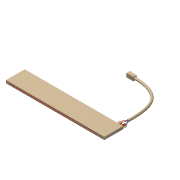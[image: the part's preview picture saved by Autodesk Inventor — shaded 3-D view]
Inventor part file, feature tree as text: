
AUTODESK INVENTOR PART (.ipt)
format: ipt  version: 2015 SP1 (Build 190203100, 203)  size: 430,080 bytes
history: native  units: mm
features: sketch x18, extrude x10, projected_geometry x10, sweep x5, plane x4, fillet x2
ambient origin geometry x8: Origin, YZ Plane, XZ Plane, XY Plane, X Axis, Y Axis, Z Axis, Center Point
bodies: Solid1 (feature_tree)
feature tree (49):
  sketch  "Sketch1"  dims[d0=210.0mm d1=40.0mm]
  extrude  "Extrusion1"  Depth=40.0mm
  extrude  "Extrusion2"  Depth=5.0mm
  extrude  "Extrusion3"  Depth=5.0mm
  extrude  "Extrusion4"  Depth=5.0mm
  extrude  "Extrusion5"  Depth=40.0mm
  extrude  "Extrusion6"  Depth=15.909903mm
  sketch  "Sketch6"  dims[d10=5.0mm d11=15.909903mm]
  plane  "Work Plane1"
  sketch  "Sketch7"  dims[d12=31.819805mm d13=15.909903mm]
  sketch  "Sketch9"  dims[d14=1.0mm d15=0.0mm d16=1.0mm d17=0.0mm]
  sketch  "Sketch10"  dims[d18=1.0mm d19=0.0mm d20=1.0mm d21=0.0mm]
  sketch  "Sketch11"  dims[d22=1.0mm d23=0.0mm d24=1.0mm d25=0.0mm]
  sketch  "Sketch12"  dims[d26=2.0mm d27=2.5mm]
  plane  "Work Plane3"
  plane  "Work Plane4"
  sketch  "Sketch13"  dims[d28=10.0mm d29=5.0mm]
  sketch  "Sketch14"  dims[d30=10.0mm d31=5.0mm]
  plane  "Work Plane5"
  sketch  "Sketch15"  dims[d32=0.8mm d33=0.8mm]
  sweep  "Sweep1"
  sweep  "Sweep2"
  sweep  "Sweep3"
  sweep  "Sweep4"
  sweep  "Sweep5"
  extrude  "Extrusion7"  Depth=5.0mm
  extrude  "Extrusion8"  Depth=5.0mm
  extrude  "Extrusion9"  Depth=0.8mm
  extrude  "Extrusion10"  Depth=0.8mm
  fillet  "Fillet1"  [1 undecoded]
  fillet  "Fillet2"  [1 undecoded]
  sketch  "Sketch2"  dims[d2=8.0mm d3=5.0mm]
  projected_geometry  "Projected Loop1"
  sketch  "Sketch3"  dims[d4=5.0mm d5=5.0mm]
  projected_geometry  "Projected Loop2"
  sketch  "Sketch4"  dims[d6=5.0mm d7=5.0mm]
  projected_geometry  "Projected Loop3"
  projected_geometry  "Projected Loop4"
  projected_geometry  "Projected Loop5"
  sketch  "Sketch5"  dims[d8=40.0mm d9=40.0mm]
  projected_geometry  "Projected Loop6"
  projected_geometry  "Projected Loop7"
  projected_geometry  "Projected Loop8"
  sketch  "Sketch16"  dims[d34=0.8mm d35=0.8mm d36=0.0mm d37=0.0mm d38=0.0mm d39=0.0mm]
  sketch  "Sketch17"  dims[d40=0.0mm d41=0.0mm]
  projected_geometry  "Projected Loop9"
  sketch  "Sketch18"  dims[d42=0.0mm d43=0.0mm]
  sketch  "Sketch19"  dims[d44=0.0mm d45=0.0mm d46=1.0mm d47=1.0mm d48=1.0mm d49=15.0mm d50=12.0mm d51=8.0mm d52=0.0mm d53=4.0mm d54=1.5mm d55=1.5mm d56=1.2mm d57=4.0mm d58=12.0mm d59=0.0mm d60=10.0mm d61=0.0mm d62=10.0mm d63=0.0mm d64=0.2mm d65=0.2mm]
  projected_geometry  "Projected Loop10"
note: 2 required parameter values undecoded (feature->parameter linkage not recoverable at this tier; creation-order binding heuristic only, values carry confidence <= 0.55)
